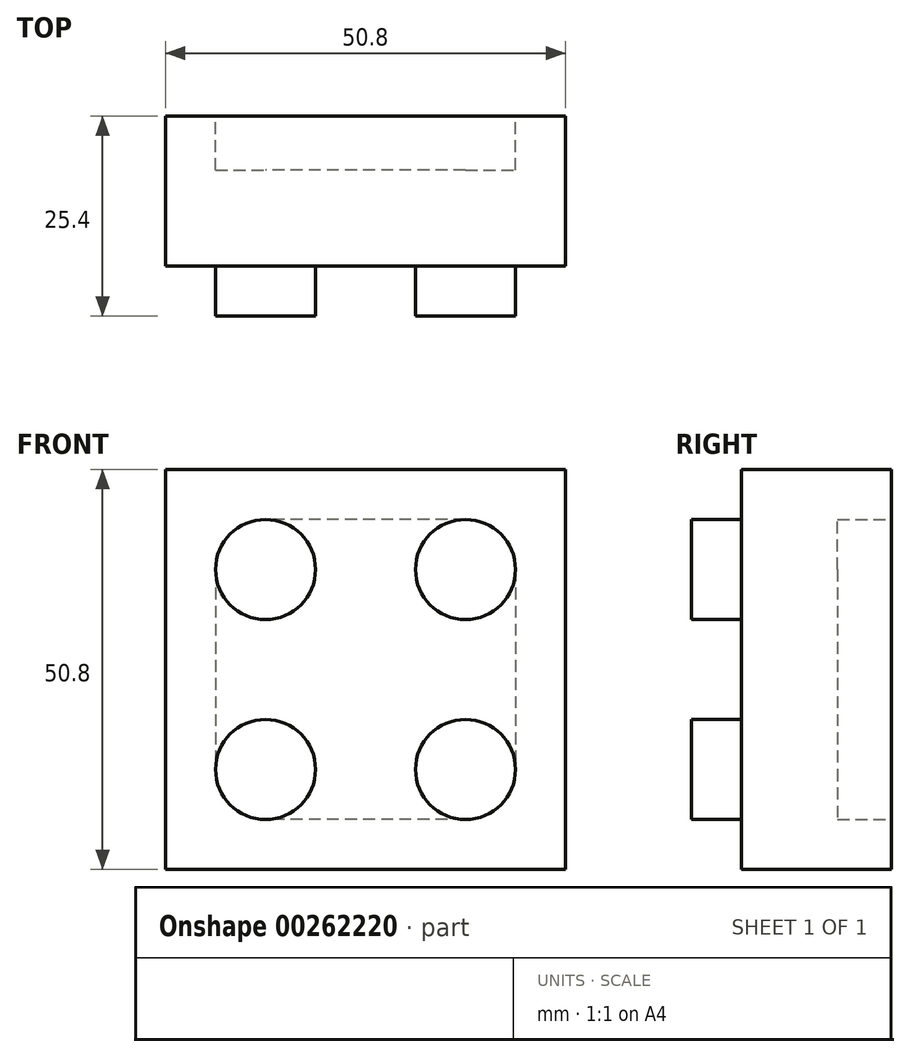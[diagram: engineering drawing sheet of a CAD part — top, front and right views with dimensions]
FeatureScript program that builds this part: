
annotation { "Feature Type Name" : "Feature", "Feature Type Description" : "" }
export const myFeature = defineFeature(function(context is Context, id is Id, definition is map)
    precondition{}
    {
        {
            var Q0;
            Q0=qCreatedBy(makeId("Front.planeOp"),FACE);
            var sketch = newSketch(context, id + "F0", { "sketchPlane" : qUnion([Q0])});
            skLineSegment(sketch, "E0.bottom", {"start": v(0, 0) * mm, "end": v(50.8, 0) * mm});
            skLineSegment(sketch, "E0.top", {"start": v(0, 50.8) * mm, "end": v(50.8, 50.8) * mm});
            skLineSegment(sketch, "E0.left", {"start": v(0, 0) * mm, "end": v(0, 50.8) * mm});
            skLineSegment(sketch, "E0.right", {"start": v(50.8, 0) * mm, "end": v(50.8, 50.8) * mm});
            skSolve(sketch);
        }
        {
            var Q0;
            Q0 = qSketchRegion(id + "F0", true);
            extrude(context, id + "F1", {"entities" : qUnion([Q0]), "depth" : 19.05 * mm});
        }
        {
            var Q0;
            Q0=makeQuery(id+"F1.opExtrude","CAP_FACE",FACE,{"disambiguationData":[OSD([sQuery(id+"F0.wireOp",EDGE,"E0.bottom"),sQuery(id+"F0.wireOp",EDGE,"E0.top"),sQuery(id+"F0.wireOp",EDGE,"E0.left"),sQuery(id+"F0.wireOp",EDGE,"E0.right")])],"isStart":false});
            var sketch = newSketch(context, id + "F2", { "sketchPlane" : qUnion([Q0])});
            skCircle(sketch, "E1", {"center": v(12.7, 38.1) * mm, "radius": 6.35 * mm});
            skCircle(sketch, "E2", {"center": v(38.1, 38.1) * mm, "radius": 6.35 * mm});
            skCircle(sketch, "E3", {"center": v(12.7, 12.7) * mm, "radius": 6.35 * mm});
            skCircle(sketch, "E4", {"center": v(38.1, 12.7) * mm, "radius": 6.35 * mm});
            skSolve(sketch);
        }
        {
            var Q0;
            Q0 = qSketchRegion(id + "F2", true);
            extrude(context, id + "F3", {"entities" : qUnion([Q0]), "operationType" : NewBodyOperationType.ADD, "depth" : 6.35 * mm});
        }
        {
            var Q0;
            Q0=makeQuery(id+"F1.opExtrude","CAP_FACE",FACE,{"disambiguationData":[OSD([sQuery(id+"F0.wireOp",EDGE,"E0.bottom"),sQuery(id+"F0.wireOp",EDGE,"E0.top"),sQuery(id+"F0.wireOp",EDGE,"E0.left"),sQuery(id+"F0.wireOp",EDGE,"E0.right")])],"isStart":true});
            var sketch = newSketch(context, id + "F4", { "sketchPlane" : qUnion([Q0])});
            skLineSegment(sketch, "E5.bottom", {"start": v(-38.1, 44.45) * mm, "end": v(-12.7, 44.45) * mm});
            skLineSegment(sketch, "E5.top", {"start": v(-38.1, 6.35) * mm, "end": v(-12.7, 6.35) * mm});
            skLineSegment(sketch, "E5.left", {"start": v(-44.45, 38.1) * mm, "end": v(-44.45, 12.7) * mm});
            skLineSegment(sketch, "E5.right", {"start": v(-6.35, 38.1) * mm, "end": v(-6.35, 12.7) * mm});
            skPoint(sketch, "E6.visualSharp", {"position": v(-44.45, 44.45) * mm});
            skArc(sketch, "E6.filletArc", {"start": v(-38.1, 44.45) * mm, "mid": v(-42.6, 42.6) * mm, "end": v(-44.45, 38.1) * mm});
            skPoint(sketch, "E7.visualSharp", {"position": v(-6.35, 44.45) * mm});
            skArc(sketch, "E7.filletArc", {"start": v(-6.35, 38.1) * mm, "mid": v(-8.2, 42.6) * mm, "end": v(-12.7, 44.45) * mm});
            skPoint(sketch, "E8.visualSharp", {"position": v(-6.35, 6.35) * mm});
            skArc(sketch, "E8.filletArc", {"start": v(-12.7, 6.35) * mm, "mid": v(-8.2, 8.2) * mm, "end": v(-6.35, 12.7) * mm});
            skPoint(sketch, "E9.visualSharp", {"position": v(-44.45, 6.35) * mm});
            skArc(sketch, "E9.filletArc", {"start": v(-44.45, 12.7) * mm, "mid": v(-42.6, 8.2) * mm, "end": v(-38.1, 6.35) * mm});
            skSolve(sketch);
        }
        {
            var Q0;
            Q0 = qSketchRegion(id + "F4", true);
            extrude(context, id + "F5", {"entities" : qUnion([Q0]), "operationType" : NewBodyOperationType.REMOVE, "oppositeDirection" : true, "depth" : 6.86 * mm});
        }
    });
